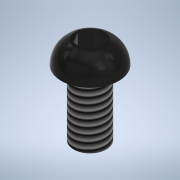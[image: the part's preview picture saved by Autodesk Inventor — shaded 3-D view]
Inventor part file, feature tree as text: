
AUTODESK INVENTOR PART (.ipt)
format: ipt  version: 2022 (Build 260153000, 153)  size: 155,648 bytes
history: native  units: mm
features: sketch x3, extrude x2, other x1, revolve x1, thread x1
ambient origin geometry x8: Origin, YZ Plane, XZ Plane, XY Plane, X Axis, Y Axis, Z Axis, Center Point
bodies: Body1 (feature_tree)
feature tree (8):
  other  "Твердое тело1"
  extrude  "Выдавливание1"  Depth=2.0mm
  revolve  "Вращение1"
  extrude  "Выдавливание2"  Depth=4.0mm TaperAngle=0.0deg
  thread  "Резьба1"
  sketch  "Эскиз1"
  sketch  "Эскиз2"
  sketch  "Эскиз3"
